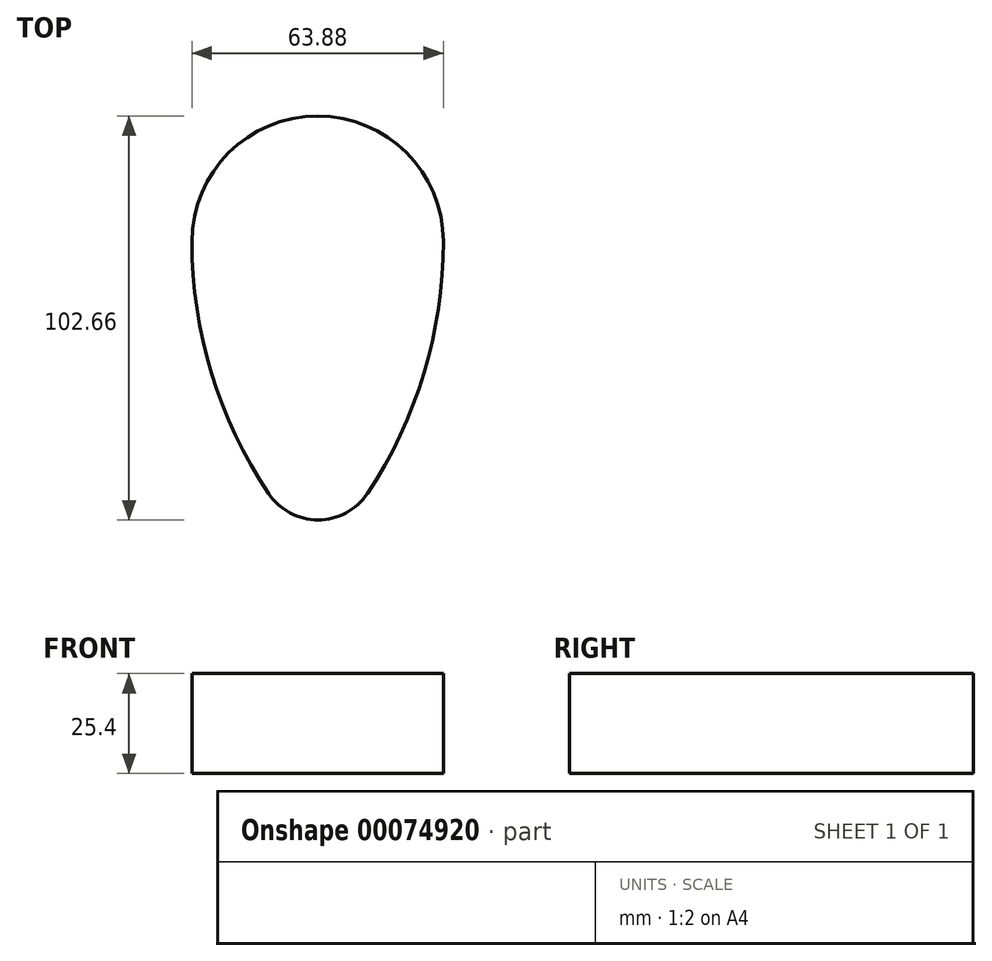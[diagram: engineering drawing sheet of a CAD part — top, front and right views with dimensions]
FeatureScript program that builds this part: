
annotation { "Feature Type Name" : "Feature", "Feature Type Description" : "" }
export const myFeature = defineFeature(function(context is Context, id is Id, definition is map)
    precondition{}
    {
        {
            var Q0;
            Q0=qCreatedBy(makeId("Top.planeOp"),FACE);
            var sketch = newSketch(context, id + "F0", { "sketchPlane" : qUnion([Q0])});
            skArc(sketch, "E0", {"start": v(-31.94, 0) * mm, "mid": v(0, 31.94) * mm, "end": v(31.94, 0) * mm});
            skArc(sketch, "E1", {"start": v(31.94, 0) * mm, "mid": v(27, -33.42) * mm, "end": v(12.63, -63.98) * mm});
            skArc(sketch, "E2", {"start": v(-31.94, 0) * mm, "mid": v(-26.97, -33.44) * mm, "end": v(-12.47, -63.98) * mm});
            skArc(sketch, "E3", {"start": v(12.63, -63.98) * mm, "mid": v(0.08, -70.72) * mm, "end": v(-12.47, -63.98) * mm});
            skSolve(sketch);
        }
        {
            var Q0;
            Q0 = qSketchRegion(id + "F0", true);
            extrude(context, id + "F1", {"entities" : qUnion([Q0]), "endBound" : BoundingType.SYMMETRIC, "depth" : 25.4 * mm});
        }
    });
